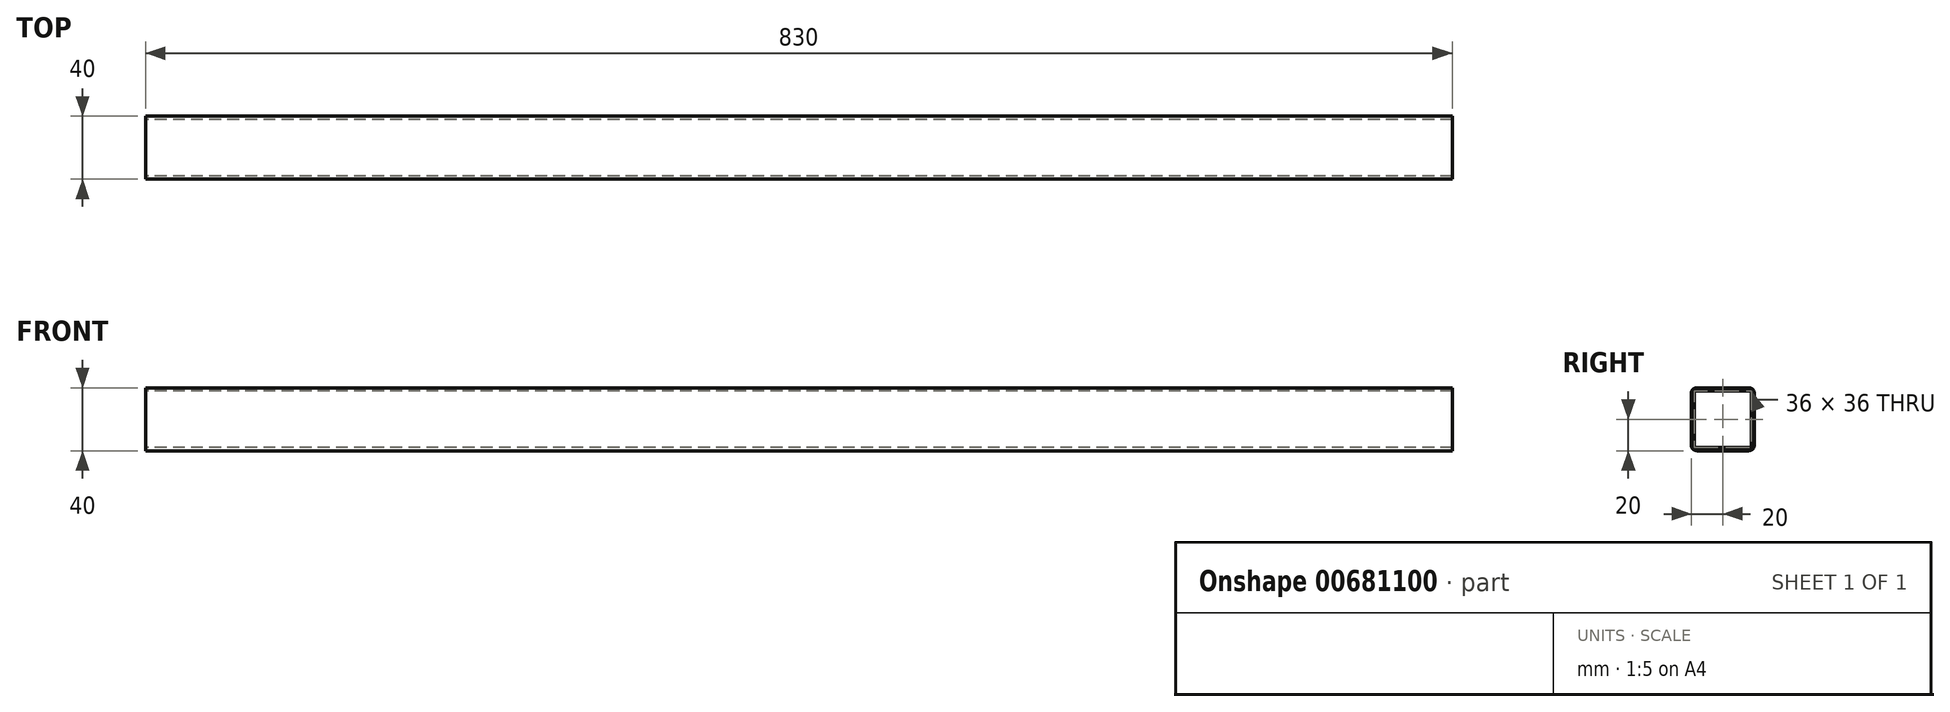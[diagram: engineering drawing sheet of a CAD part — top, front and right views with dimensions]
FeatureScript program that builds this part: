
annotation { "Feature Type Name" : "Feature", "Feature Type Description" : "" }
export const myFeature = defineFeature(function(context is Context, id is Id, definition is map)
    precondition{}
    {
        {
            var Q0;
            Q0=qCreatedBy(makeId("Right.planeOp"),FACE);
            var sketch = newSketch(context, id + "F0", { "sketchPlane" : qUnion([Q0])});
            skLineSegment(sketch, "E0.bottom", {"start": v(16.5, 20) * mm, "end": v(-16.5, 20) * mm});
            skLineSegment(sketch, "E0.top", {"start": v(16.5, -20) * mm, "end": v(-16.5, -20) * mm});
            skLineSegment(sketch, "E0.left", {"start": v(20, 16.5) * mm, "end": v(20, -16.5) * mm});
            skLineSegment(sketch, "E0.right", {"start": v(-20, 16.5) * mm, "end": v(-20, -16.5) * mm});
            skPoint(sketch, "E0.middle", {"position": v(0, 0) * mm});
            skLineSegment(sketch, "E1.bottom", {"start": v(18, 18) * mm, "end": v(-18, 18) * mm});
            skLineSegment(sketch, "E1.top", {"start": v(18, -18) * mm, "end": v(-18, -18) * mm});
            skLineSegment(sketch, "E1.left", {"start": v(18, 18) * mm, "end": v(18, -18) * mm});
            skLineSegment(sketch, "E1.right", {"start": v(-18, 18) * mm, "end": v(-18, -18) * mm});
            skPoint(sketch, "E2.visualSharp", {"position": v(-20, 20) * mm});
            skArc(sketch, "E2.filletArc", {"start": v(-16.5, 20) * mm, "mid": v(-18.97, 18.97) * mm, "end": v(-20, 16.5) * mm});
            skPoint(sketch, "E3.visualSharp", {"position": v(20, 20) * mm});
            skArc(sketch, "E3.filletArc", {"start": v(20, 16.5) * mm, "mid": v(18.97, 18.97) * mm, "end": v(16.5, 20) * mm});
            skPoint(sketch, "E4.visualSharp", {"position": v(20, -20) * mm});
            skArc(sketch, "E4.filletArc", {"start": v(16.5, -20) * mm, "mid": v(18.97, -18.97) * mm, "end": v(20, -16.5) * mm});
            skPoint(sketch, "E5.visualSharp", {"position": v(-20, -20) * mm});
            skArc(sketch, "E5.filletArc", {"start": v(-20, -16.5) * mm, "mid": v(-18.97, -18.97) * mm, "end": v(-16.5, -20) * mm});
            skSolve(sketch);
        }
        {
            var Q0;
            Q0=makeQuery(id+"F0.imprint","IMPRINT",FACE,{"disambiguationData":[TD([[makeQuery(id+"F0.imprint","IMPRINT",EDGE,{"derivedFrom":sQuery(id+"F0.wireOp",EDGE,"E0.bottom")}),1.0]])]});
            extrude(context, id + "F1", {"entities" : qUnion([Q0]), "depth" : 830 * mm, "offsetDistance" : 25 * mm});
        }
    });
